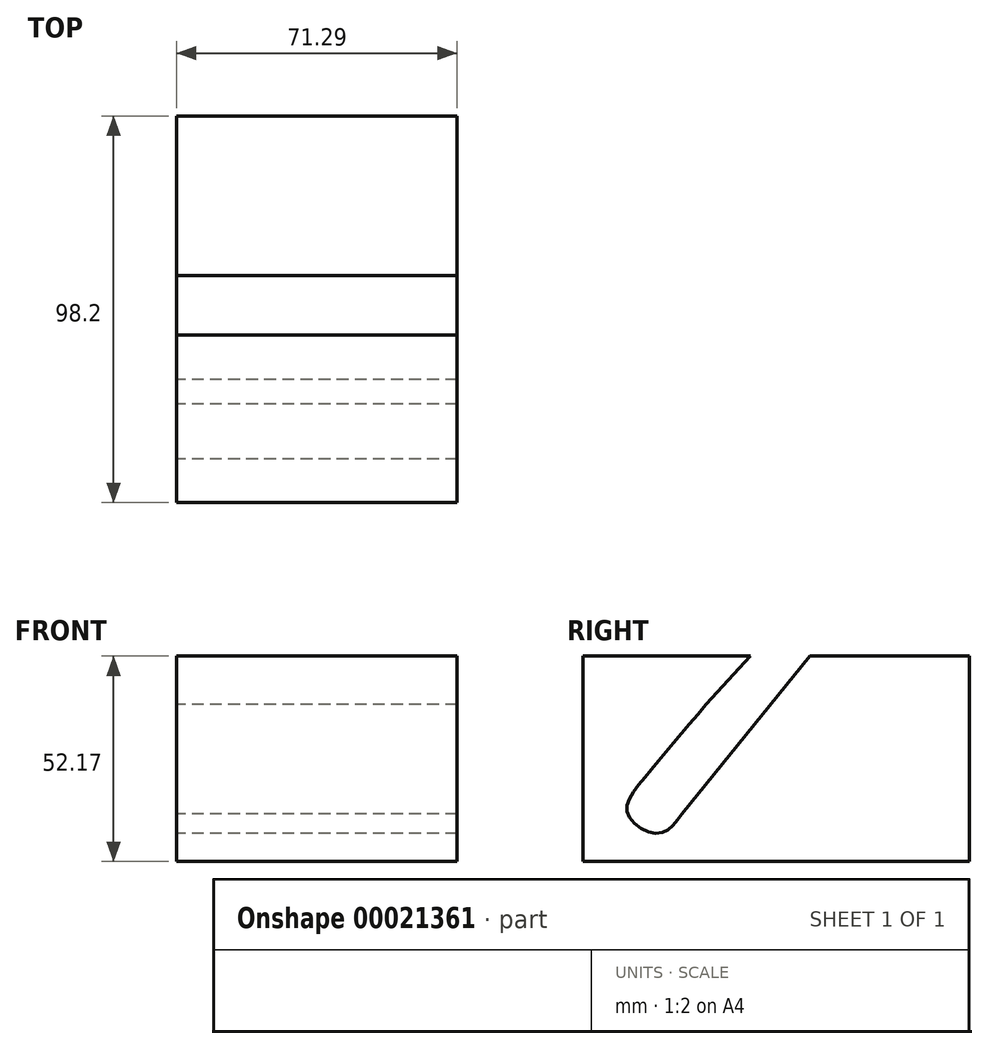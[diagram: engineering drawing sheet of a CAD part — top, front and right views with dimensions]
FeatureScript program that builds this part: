
annotation { "Feature Type Name" : "Feature", "Feature Type Description" : "" }
export const myFeature = defineFeature(function(context is Context, id is Id, definition is map)
    precondition{}
    {
        {
            var Q0;
            Q0=qCreatedBy(makeId("Right.planeOp"),FACE);
            var sketch = newSketch(context, id + "F0", { "sketchPlane" : qUnion([Q0])});
            skLineSegment(sketch, "E0", {"start": v(-52.34, 0) * mm, "end": v(-52.34, -52.17) * mm});
            skLineSegment(sketch, "E1", {"start": v(-52.34, -52.17) * mm, "end": v(45.86, -52.17) * mm});
            skLineSegment(sketch, "E2", {"start": v(45.86, -52.17) * mm, "end": v(45.86, 0) * mm});
            skLineSegment(sketch, "E3", {"start": v(45.86, 0) * mm, "end": v(5.32, 0) * mm});
            skLineSegment(sketch, "E4", {"start": v(5.32, 0) * mm, "end": v(-27.25, -40.04) * mm});
            skFitSpline(sketch, "E5", {"points": [v(-27.25, -40.04) * mm, v(-33.23, -45.03) * mm, v(-41.04, -40.04) * mm, v(-37.05, -31.24) * mm, v(-21.1, -12.3) * mm], "startDerivative": vector(-25.1, -36.16) * mm, "endDerivative": vector(48.47, 57.02) * mm});
            skLineSegment(sketch, "E6", {"start": v(-21.1, -12.3) * mm, "end": v(-9.8, 0) * mm});
            skLineSegment(sketch, "E7", {"start": v(-9.8, 0) * mm, "end": v(-52.34, 0) * mm});
            skSolve(sketch);
        }
        {
            var Q0;
            Q0=makeQuery(id+"F0.imprint","IMPRINT",FACE,{"disambiguationData":[TD([[makeQuery(id+"F0.imprint","IMPRINT",EDGE,{"derivedFrom":sQuery(id+"F0.wireOp",EDGE,"E0")}),1.0]])]});
            extrude(context, id + "F1", {"entities" : qUnion([Q0]), "depth" : 28.78 * mm});
        }
        {
            var Q0;
            Q0=makeQuery(id+"F1.opExtrude","CAP_FACE",FACE,{"disambiguationData":[OSD([sQuery(id+"F0.wireOp",EDGE,"E0"),sQuery(id+"F0.wireOp",EDGE,"E1"),sQuery(id+"F0.wireOp",EDGE,"E2"),sQuery(id+"F0.wireOp",EDGE,"E3"),sQuery(id+"F0.wireOp",EDGE,"E4"),sQuery(id+"F0.wireOp",EDGE,"E5"),sQuery(id+"F0.wireOp",EDGE,"E6"),sQuery(id+"F0.wireOp",EDGE,"E7")])],"isStart":false});
            extrude(context, id + "F2", {"entities" : qUnion([Q0]), "operationType" : NewBodyOperationType.ADD, "depth" : 42.5 * mm});
        }
    });
